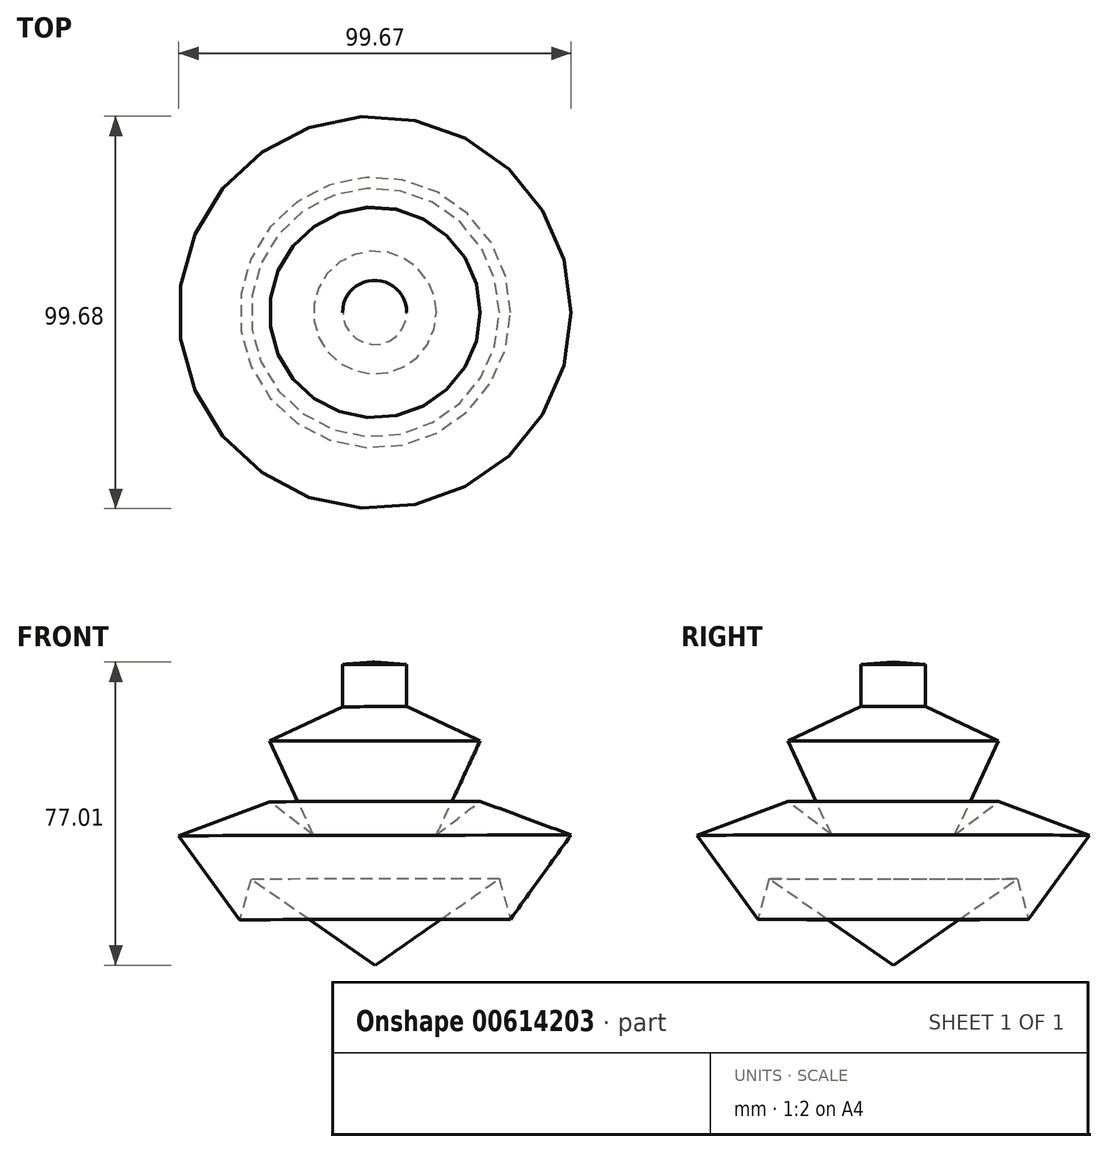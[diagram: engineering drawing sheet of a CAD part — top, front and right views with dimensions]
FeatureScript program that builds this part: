
annotation { "Feature Type Name" : "Feature", "Feature Type Description" : "" }
export const myFeature = defineFeature(function(context is Context, id is Id, definition is map)
    precondition{}
    {
        {
            var Q0;
            Q0=qCreatedBy(makeId("Front.planeOp"),FACE);
            var sketch = newSketch(context, id + "F0", { "sketchPlane" : qUnion([Q0])});
            skLineSegment(sketch, "E0", {"start": v(0, 0) * mm, "end": v(31.52, 21.96) * mm});
            skLineSegment(sketch, "E1", {"start": v(31.52, 21.96) * mm, "end": v(34.37, 11.7) * mm});
            skLineSegment(sketch, "E2", {"start": v(34.37, 11.7) * mm, "end": v(49.77, 33.09) * mm});
            skLineSegment(sketch, "E3", {"start": v(49.77, 33.09) * mm, "end": v(26.67, 41.65) * mm});
            skLineSegment(sketch, "E4", {"start": v(26.67, 41.65) * mm, "end": v(15.55, 33.09) * mm});
            skLineSegment(sketch, "E5", {"start": v(15.55, 33.09) * mm, "end": v(26.67, 57.05) * mm});
            skLineSegment(sketch, "E6", {"start": v(26.67, 57.05) * mm, "end": v(8.02, 65.7) * mm});
            skLineSegment(sketch, "E7", {"start": v(8.02, 65.7) * mm, "end": v(8.02, 76.44) * mm});
            skLineSegment(sketch, "E8", {"start": v(8.02, 76.44) * mm, "end": v(-0.14, 77.01) * mm});
            skLineSegment(sketch, "E9", {"start": v(-0.14, 77.01) * mm, "end": v(0, 0) * mm});
            skSolve(sketch);
        }
        {
            var Q0;
            Q0=makeQuery(id+"F0.imprint","IMPRINT",FACE,{"disambiguationData":[TD([[makeQuery(id+"F0.imprint","IMPRINT",EDGE,{"derivedFrom":sQuery(id+"F0.wireOp",EDGE,"E0")}),1.0]])]});
            var Q1;
            Q1=sQuery(id+"F0.wireOp",EDGE,"E9");
            revolve(context, id + "F1", {"entities" : qUnion([Q0]), "axis" : qUnion([Q1]), "revolveType" : RevolveType.FULL});
        }
    });
